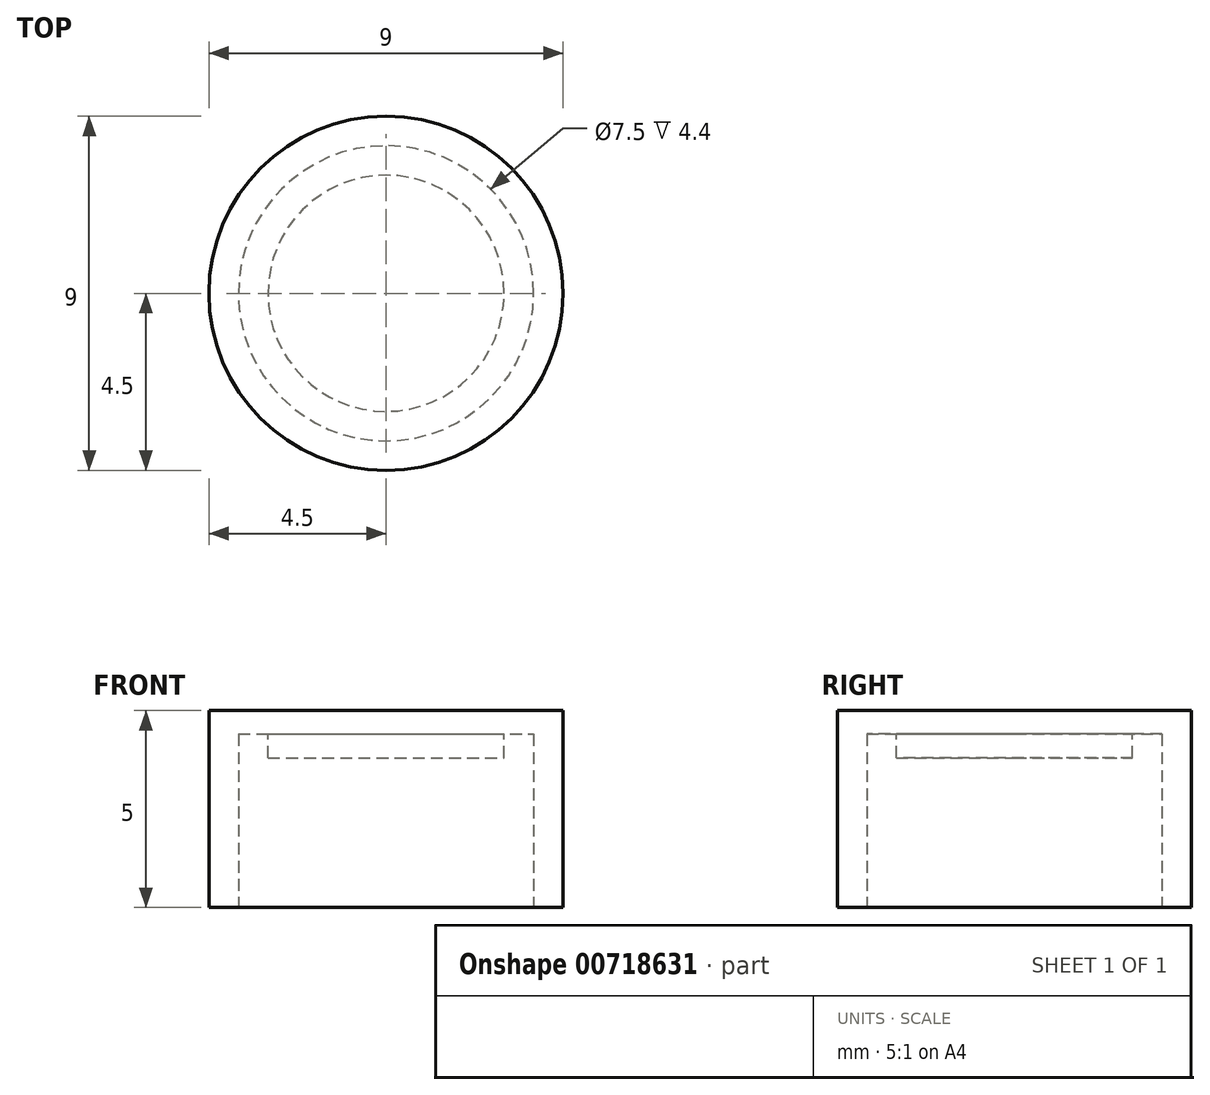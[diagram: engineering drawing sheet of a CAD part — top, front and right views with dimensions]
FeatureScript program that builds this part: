
annotation { "Feature Type Name" : "Feature", "Feature Type Description" : "" }
export const myFeature = defineFeature(function(context is Context, id is Id, definition is map)
    precondition{}
    {
        {
            var Q0;
            Q0=qCreatedBy(makeId("Top.planeOp"),FACE);
            var sketch = newSketch(context, id + "F0", { "sketchPlane" : qUnion([Q0])});
            skCircle(sketch, "E0", {"center": v(0, 0) * mm, "radius": 4.5 * mm});
            skSolve(sketch);
        }
        {
            var Q0;
            Q0=makeQuery(id+"F0.imprint","IMPRINT",FACE,{"disambiguationData":[TD([[makeQuery(id+"F0.imprint","IMPRINT",EDGE,{"derivedFrom":sQuery(id+"F0.wireOp",EDGE,"E0")}),1.0]])]});
            extrude(context, id + "F1", {"entities" : qUnion([Q0]), "depth" : 5 * mm, "offsetDistance" : 25 * mm});
        }
        {
            var Q0;
            Q0=makeQuery(id+"F1.opExtrude","CAP_FACE",FACE,{"disambiguationData":[OSD([sQuery(id+"F0.wireOp",EDGE,"E0")])],"isStart":true});
            var sketch = newSketch(context, id + "F2", { "sketchPlane" : qUnion([Q0])});
            skCircle(sketch, "E1", {"center": v(0, 0) * mm, "radius": 3.75 * mm});
            skSolve(sketch);
        }
        {
            var Q0;
            Q0 = qSketchRegion(id + "F2", true);
            extrude(context, id + "F3", {"entities" : qUnion([Q0]), "operationType" : NewBodyOperationType.REMOVE, "oppositeDirection" : true, "depth" : 4.4 * mm, "offsetDistance" : 25 * mm});
        }
        {
            var Q0;
            Q0=makeQuery(id+"F3.boolean.opBoolean","COPY",FACE,{"derivedFrom":makeQuery(id+"F3.opExtrude","CAP_FACE",FACE,{"disambiguationData":[OSD([sQuery(id+"F2.wireOp",EDGE,"E1")])],"isStart":false})});
            var sketch = newSketch(context, id + "F4", { "sketchPlane" : qUnion([Q0])});
            skCircle(sketch, "E2", {"center": v(0, 0) * mm, "radius": 3 * mm});
            skSolve(sketch);
        }
        {
            var Q0;
            Q0 = qSketchRegion(id + "F4", true);
            extrude(context, id + "F5", {"entities" : qUnion([Q0]), "operationType" : NewBodyOperationType.ADD, "depth" : 0.6 * mm, "offsetDistance" : 25 * mm});
        }
    });
